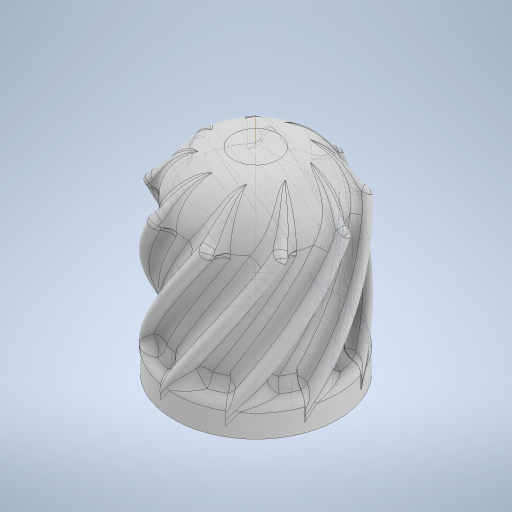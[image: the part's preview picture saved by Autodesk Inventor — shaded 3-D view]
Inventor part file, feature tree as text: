
AUTODESK INVENTOR PART (.ipt)
format: ipt  version: 2023 (Build 270158030, 158C)  size: 2,113,536 bytes
history: native  units: mm
features: fillet x6, sketch x4, projected_geometry x4, extrude x3, helix x1, pattern_circular x1
ambient origin geometry x8: Origin, YZ Plane, XZ Plane, XY Plane, X Axis, Y Axis, Z Axis, Center Point
bodies: Solid1 (feature_tree)
feature tree (19):
  extrude  "Extrusion1"  Depth=16.5mm TaperAngle=0.0deg
  extrude  "Extrusion2"  Depth=7.1mm
  extrude  "Extrusion3"  Depth=3.55mm
  fillet  "Fillet1"  Radius=13.2mm
  helix  "Coil1"  [1 undecoded]
  fillet  "Fillet3"  Radius=13.8mm
  fillet  "Fillet2"  Radius=2.4mm
  pattern_circular  "Circular Pattern1"  [2 undecoded]
  fillet  "Fillet5"  Radius=1.0mm
  fillet  "Fillet6"  Radius=0.1mm
  fillet  "Fillet4"  Radius=90.0mm
  sketch  "Sketch1"  dims[d0=13.85mm d1=16.5mm d2=0.0mm]
  sketch  "Sketch2"  dims[d3=7.1mm d4=7.1mm]
  sketch  "Sketch3"  dims[d5=3.55mm d6=3.55mm d7=13.2mm d8=0.0mm d9=11.6mm d10=13.8mm d11=0.0mm d12=2.4mm]
  projected_geometry  "Projected Loop1"
  sketch  "Sketch4"  dims[d13=1.2mm d14=70.0mm d15=12.0mm d16=2.0mm d17=0.0mm d18=90.0deg d19=90.0deg d20=0.0mm d21=0.174533mm d22=3.9mm d23=0.9mm d24=1.0mm d25=0.1mm d26=90.0mm d27=360.0deg d29=0.5mm d30=0.5mm]
  projected_geometry  "Projected Loop2"
  projected_geometry  "Projected Loop3"
  projected_geometry  "Projected Loop4"
note: 3 required parameter values undecoded (feature->parameter linkage not recoverable at this tier; creation-order binding heuristic only, values carry confidence <= 0.55)
